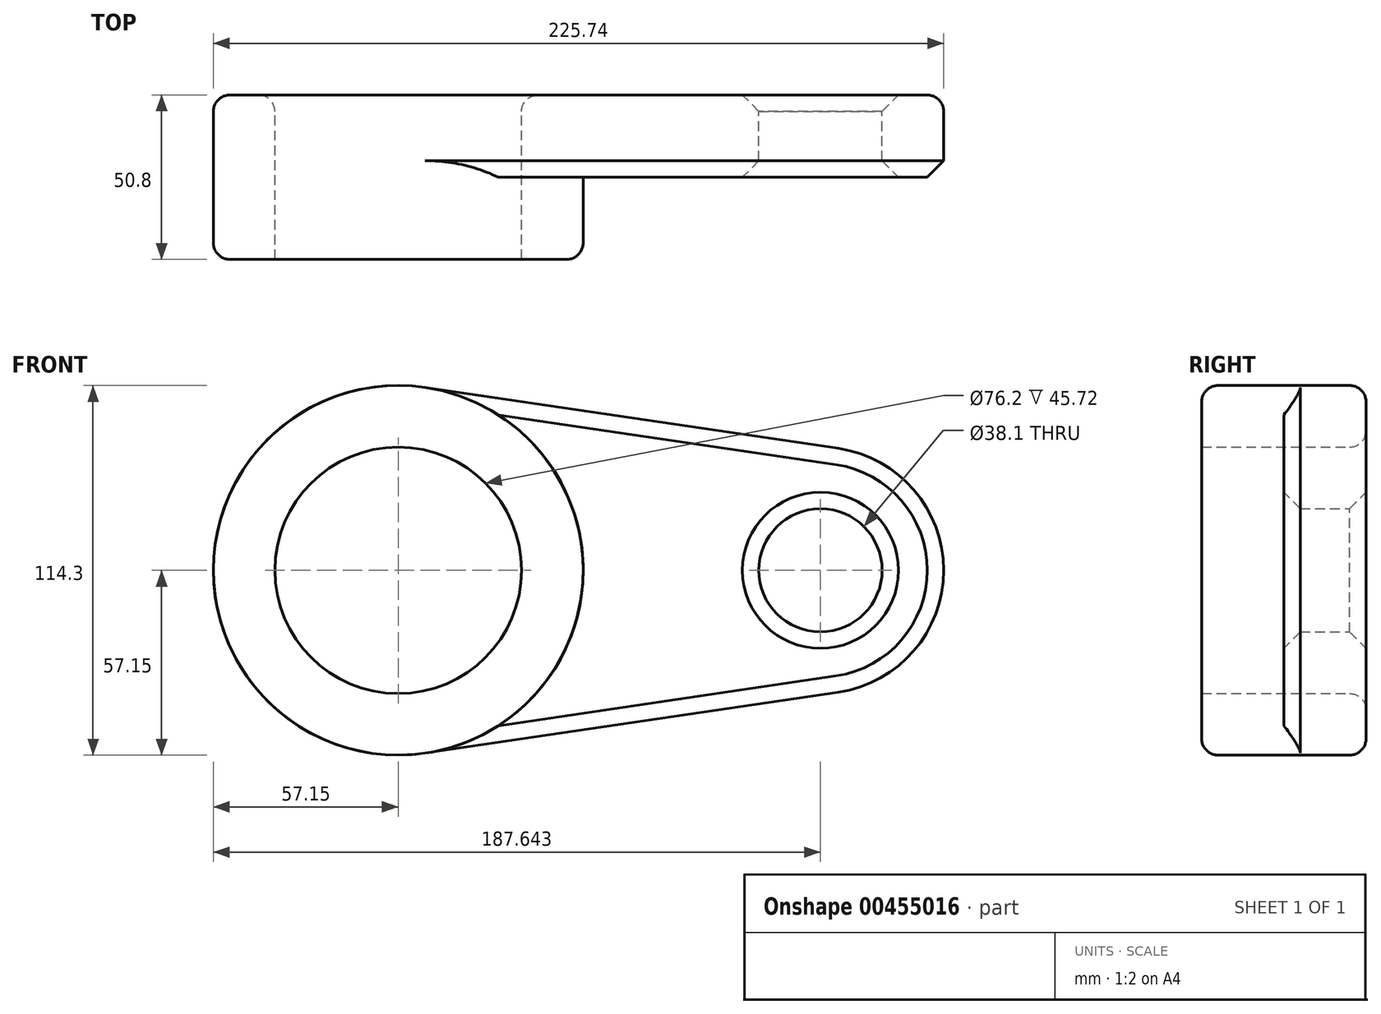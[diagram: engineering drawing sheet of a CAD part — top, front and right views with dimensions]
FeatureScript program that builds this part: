
annotation { "Feature Type Name" : "Feature", "Feature Type Description" : "" }
export const myFeature = defineFeature(function(context is Context, id is Id, definition is map)
    precondition{}
    {
        {
            var Q0;
            Q0=qCreatedBy(makeId("Front.planeOp"),FACE);
            var sketch = newSketch(context, id + "F0", { "sketchPlane" : qUnion([Q0])});
            skCircle(sketch, "E0", {"center": v(0, 0) * mm, "radius": 57.15 * mm});
            skCircle(sketch, "E1", {"center": v(130.5, 0) * mm, "radius": 38.1 * mm});
            skLineSegment(sketch, "E2", {"start": v(8.34, 56.54) * mm, "end": v(136.05, 37.7) * mm});
            skLineSegment(sketch, "E3", {"start": v(8.34, -56.54) * mm, "end": v(136.05, -37.7) * mm});
            skCircle(sketch, "E4", {"center": v(0, 0) * mm, "radius": 38.1 * mm});
            skCircle(sketch, "E5", {"center": v(130.5, 0) * mm, "radius": 19.05 * mm});
            skSolve(sketch);
        }
        {
            var Q0;
            Q0 = qSketchRegion(id + "F0", true);
            extrude(context, id + "F1", {"entities" : qUnion([Q0]), "depth" : 25.4 * mm});
        }
        {
            var Q0;
            Q0=makeQuery(id+"F0.imprint","IMPRINT",FACE,{"disambiguationData":[TD([[makeQuery(id+"F0.imprint","IMPRINT",EDGE,{"derivedFrom":sQuery(id+"F0.wireOp",EDGE,"E4")}),-1.0]])]});
            extrude(context, id + "F2", {"entities" : qUnion([Q0]), "operationType" : NewBodyOperationType.ADD, "depth" : 50.8 * mm});
        }
        {
            var Q0;
            Q0=makeQuery(id+"F2.opExtrude","CAP_EDGE",EDGE,{"disambiguationData":[OSD([sQuery(id+"F0.wireOp",EDGE,"E0")])],"isStart":false});
            var Q1;
            Q1=makeQuery(id+"F1.opExtrude","CAP_EDGE",EDGE,{"disambiguationData":[OSD([sQuery(id+"F0.wireOp",EDGE,"E4")])],"isStart":true});
            var Q2;
            Q2=makeQuery(id+"F1.opExtrude","CAP_EDGE",EDGE,{"disambiguationData":[OSD([sQuery(id+"F0.wireOp",EDGE,"E0")])],"isStart":true});
            fillet(context, id + "F3", {"entities" : qUnion([Q0, Q1, Q2]), "radius" : 5.08 * mm, "tangentPropagation" : true, "allowEdgeOverflow" : false});
        }
        {
            var Q0;
            Q0=makeQuery(id+"F1.opExtrude","SWEPT_FACE",FACE,{"disambiguationData":[OSD([sQuery(id+"F0.wireOp",EDGE,"E5")])]});
            var Q1;
            Q1=makeQuery(id+"F1.opExtrude","CAP_EDGE",EDGE,{"disambiguationData":[OSD([sQuery(id+"F0.wireOp",EDGE,"E2")])],"isStart":false});
            chamfer(context, id + "F4", {"entities" : qUnion([Q0, Q1]), "width" : 5.08 * mm, "tangentPropagation" : true});
        }
    });
